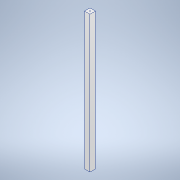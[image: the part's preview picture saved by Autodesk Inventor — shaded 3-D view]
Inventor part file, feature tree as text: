
AUTODESK INVENTOR PART (.ipt)
format: ipt  version: 2020 (Build 240168000, 168)  size: 108,032 bytes
history: native  units: mm
features: sketch x2, other x1, extrude x1, hole x1
ambient origin geometry x8: Origin, YZ Plane, XZ Plane, XY Plane, X Axis, Y Axis, Z Axis, Center Point
bodies: Solid1 (feature_tree)
feature tree (5):
  other  "<userpath>\Documents\Development\paragon-printer\Paragon Printer Parameters.xlsx"
  extrude  "Extrusion1"  Depth=20.0mm
  hole  "Hole1"  [1 undecoded]
  sketch  "Sketch1"  dims[d0=20.0mm d1=20.0mm]
  sketch  "Sketch2"  dims[d2=500.0mm d3=0.0mm d4=3.4mm d5=6.0mm d6=6.3mm d7=2.0mm d8=90.0deg d9=8.0mm d10=20.594885mm]
note: 1 required parameter value undecoded (feature->parameter linkage not recoverable at this tier; creation-order binding heuristic only, values carry confidence <= 0.55)
